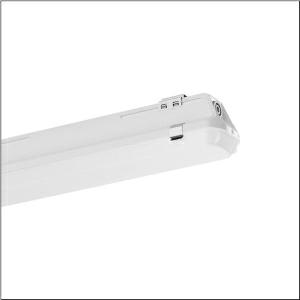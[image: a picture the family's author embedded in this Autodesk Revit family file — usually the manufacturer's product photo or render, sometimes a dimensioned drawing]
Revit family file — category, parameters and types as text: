
# Revit family: monsun_r__11_51fp209p460h_6055
name_source: partatom
category: Lighting Fixtures
units: mm (PartAtom-declared; Revit-internal decimal feet)

## family parameters
Cut with Voids When Loaded = No
Host = Face
Light Source = No
Part Type = Normal
Room Calculation Point = No
Round Connector Dimension = Use Diameter
Shared = No

## types (1)
- Monsun® 11 (1 x LED, 5490 lm, 34 W, 4000K)
    Apparent Load = 34 VA
    CIE Flux Codes = 45 75 93 94 100
    Color Rendering = 80
    Color Temperature = 4000K
    Default Elevation = 1800 mm
    Description = Monsun® 11, damp-proof luminaire, chain hanger, primary optical cover: enclosure, of PC, light emission: direct distribution, primary light characteristic: symmetric, installation type: suspended mounting, surface-mounted, horizontal mounting, vertical mounting, LED, rated luminous flux: 5.490lm, luminous efficacy: 161lm/W, light colour: 840, colour temperature: 4000K, control gear: ECG, with terminal, 3-pole, max. 2.5mm², mains connection: 220..240V, AC, 50/60Hz, rated input power: 34W, luminaire housing, of glass-fibre reinforced polyester, uncoated, bright grey, incl. chain hanger, length: 1.590mm, width: 90mm, height: 88mm, clip for enclosure, of stainless steel (V2A), ceiling mounting element, of stainless steel (V2A), chain hanger, of stainless steel (V2A), protection rating (complete): IP66, insulation class (complete): insulation class I (protective earthing), certification: CE, ENEC, VDE, UKCA, protection symbol: D, impact resistance: IK08, permissible operating ambient temperature: -35..+40°C, standard: EN 50419, EN 60598-2-1, no direct snow, no direct sun, no direct rain, for indoor or canopied outdoor use, corresponds to IFS (International Featured Standards) requirements for safety and quality in the food industry, contact your sales advisor before using the luminaires in applications with unclear chemical exposure, large temperature fluctuations or condensation-forming humidity, LABS conformity tested according to VDMA 24364:2018-05, packaging unit: 1 piece
    Height = 89 mm
    Lamp = 1 x LED
    Lamp Light Flux = 5490 lm
    Lamp Power = 34 W
    Lamp count = 1
    Length = 1590 mm
    Luminous efficacy = 161 lm/W
    Manufacturer = Siteco
    ModVariant = No
    Model = 51FP209P460H
    Mounting Place = Ceiling
    Mounting Type = Surface mounted
    Number of Poles = 1
    OnlyDefault = Yes
    Power Factor = 1
    Product Name = Monsun® 11
    Product group = damp-proof luminaire
    ProductGroupID = 301
    Protection Class = Protection class I
    Protection Degree = IP 66
    RLX_Detail_Level = 1
    RLX_Emergency_Light_Flux = 0 lm
    RLX_Emergency_Type = 0
    RLX_Emergency_Type_DB = No
    RlxData = <blob elided: 88913 chars, md5=90728be5>
    Socket = socket
    Standby Power = 0 W
    System Light Flux = 5490 lm
    System Power = 34 W
    Type Comments = Product without accessories
    Type Image = l_1004748.jpg
    URL = http://relux.com
    VarID = ---
    Voltage = 0 V
    Weight = 0.00 kg
    Width = 90 mm

## geometry (parser evidence)
native form markers: Blend x4, Sweep x14
no freeform markers — native parametric forms only
